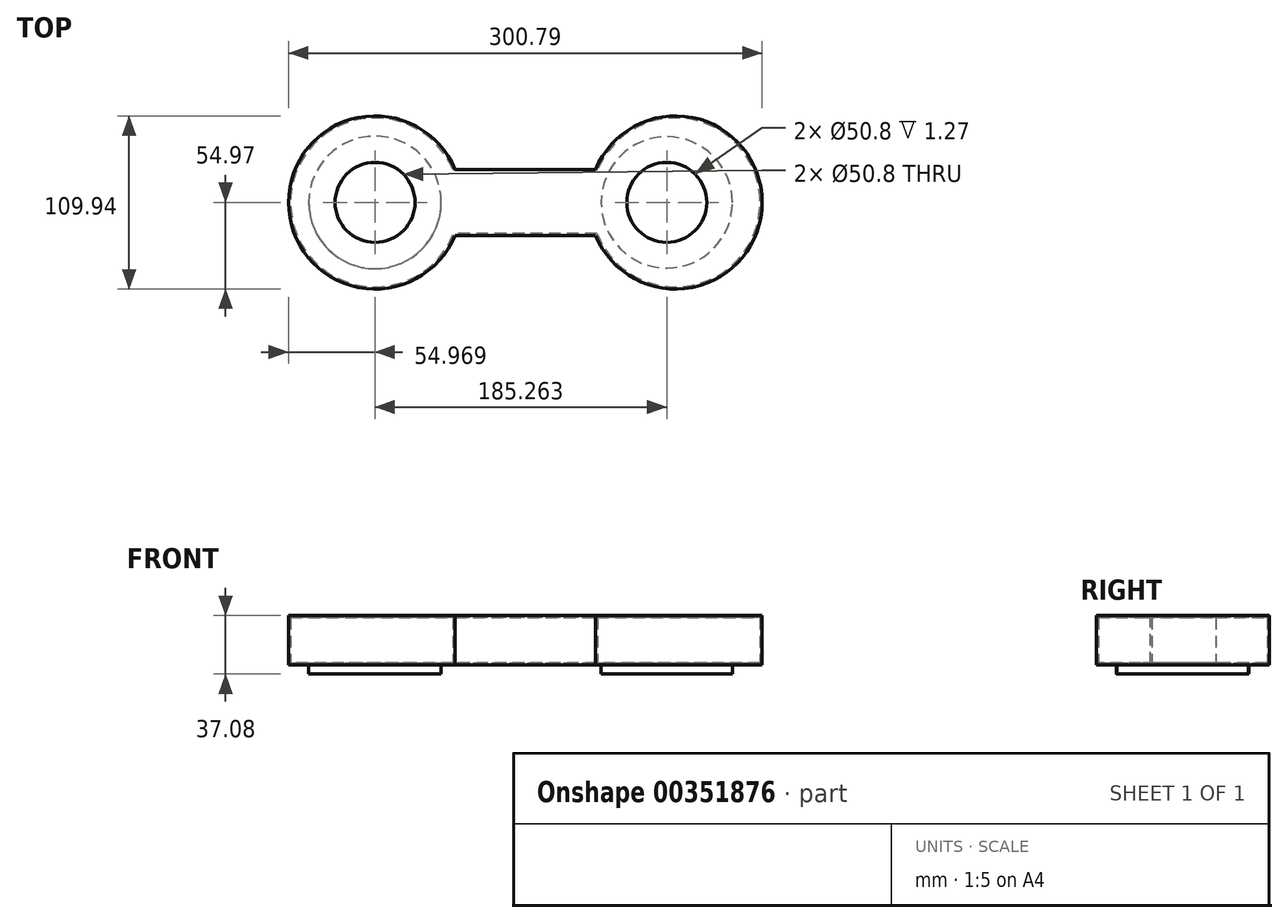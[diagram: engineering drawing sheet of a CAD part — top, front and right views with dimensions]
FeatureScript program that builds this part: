
annotation { "Feature Type Name" : "Feature", "Feature Type Description" : "" }
export const myFeature = defineFeature(function(context is Context, id is Id, definition is map)
    precondition{}
    {
        {
            var Q0;
            Q0=qCreatedBy(makeId("Top.planeOp"),FACE);
            var sketch = newSketch(context, id + "F0", { "sketchPlane" : qUnion([Q0])});
            skCircle(sketch, "E0", {"center": v(-92.63, 0) * mm, "radius": 54.97 * mm});
            skCircle(sketch, "E1.MirrorC", {"center": v(98.22, 0) * mm, "radius": 54.97 * mm});
            skLineSegment(sketch, "E2", {"start": v(-61.85, 20.9) * mm, "end": v(61.85, 20.9) * mm});
            skLineSegment(sketch, "E3", {"start": v(59.82, 20.9) * mm, "end": v(59.82, -20.9) * mm});
            skLineSegment(sketch, "E4", {"start": v(61.85, -20.9) * mm, "end": v(-61.85, -20.9) * mm});
            skLineSegment(sketch, "E5", {"start": v(-51.43, -20.9) * mm, "end": v(-51.43, 20.9) * mm});
            skSolve(sketch);
        }
        {
            var Q0;
            {var subQ0=sQuery(id+"F0.wireOp",EDGE,"E5");Q0=makeQuery(id+"F0.imprint","IMPRINT",FACE,{"disambiguationData":[TD([[makeQuery(id+"F0.imprint","IMPRINT",EDGE,{"derivedFrom":subQ0}),1.0]])]});}
            var Q1;
            {var subQ1=sQuery(id+"F0.wireOp",EDGE,"E2");Q1=makeQuery(id+"F0.imprint","IMPRINT",FACE,{"disambiguationData":[TD([[makeQuery(id+"F0.imprint","IMPRINT",EDGE,{"derivedFrom":subQ1}),-1.0]])]});}
            var Q2;
            {var subQ0=sQuery(id+"F0.wireOp",EDGE,"E3");Q2=makeQuery(id+"F0.imprint","IMPRINT",FACE,{"disambiguationData":[TD([[makeQuery(id+"F0.imprint","IMPRINT",EDGE,{"derivedFrom":subQ0}),1.0]])]});}
            var Q3;
            {var subQ0=sQuery(id+"F0.wireOp",EDGE,"E3");Q3=makeQuery(id+"F0.imprint","IMPRINT",FACE,{"disambiguationData":[TD([[makeQuery(id+"F0.imprint","IMPRINT",EDGE,{"derivedFrom":subQ0}),-1.0]])]});}
            var Q4;
            {var subQ0=sQuery(id+"F0.wireOp",EDGE,"E5");Q4=makeQuery(id+"F0.imprint","IMPRINT",FACE,{"disambiguationData":[TD([[makeQuery(id+"F0.imprint","IMPRINT",EDGE,{"derivedFrom":subQ0}),-1.0]])]});}
            extrude(context, id + "F1", {"entities" : qUnion([Q0, Q1, Q2, Q3, Q4]), "depth" : 31.24 * mm});
        }
        {
            var Q0;
            Q0=makeQuery(id+"F1.opExtrude","SWEPT_FACE",FACE,{"disambiguationData":[OSD([sQuery(id+"F0.wireOp",EDGE,"E2")])]});
            shell(context, id + "F2", {"entities" : qUnion([Q0]), "thickness" : 1.27 * mm});
        }
        {
            var Q0;
            Q0=makeQuery(id+"F1.opExtrude","CAP_FACE",FACE,{"disambiguationData":[OSD([sQuery(id+"F0.wireOp",EDGE,"E0"),sQuery(id+"F0.wireOp",EDGE,"E1.MirrorC"),sQuery(id+"F0.wireOp",EDGE,"E2"),sQuery(id+"F0.wireOp",EDGE,"E4")])],"isStart":false});
            var sketch = newSketch(context, id + "F3", { "sketchPlane" : qUnion([Q0])});
            skPoint(sketch, "E6", {"position": v(-92.63, 0) * mm});
            skPoint(sketch, "E7.MirrorP", {"position": v(92.63, 0) * mm});
            skSolve(sketch);
        }
        {
            var Q0;
            Q0=sQuery(id+"F3.wireOp",VERTEX,"E6");
            var Q1;
            Q1=sQuery(id+"F3.wireOp",VERTEX,"E7.MirrorP");
            var Q2;
            Q2=makeQuery(id+"F1.opExtrude","SWEPT_BODY",BODY,{"disambiguationData":[OSD([sQuery(id+"F0.wireOp",EDGE,"E0"),sQuery(id+"F0.wireOp",EDGE,"E1.MirrorC"),sQuery(id+"F0.wireOp",EDGE,"E2"),sQuery(id+"F0.wireOp",EDGE,"E4")])]});
            hole(context, id + "F4", {"style" : HoleStyle.SIMPLE, "endStyle" : HoleEndStyle.THROUGH, "holeDiameter" : 50.8 * mm, "isTappedThrough" : true, "tappedDepth" : 12.7 * mm, "tapClearance" : 3, "locations" : qUnion([Q0, Q1]), "scope" : qUnion([Q2])});
        }
        {
            var Q0;
            Q0=makeQuery(id+"F1.opExtrude","CAP_FACE",FACE,{"disambiguationData":[OSD([sQuery(id+"F0.wireOp",EDGE,"E0"),sQuery(id+"F0.wireOp",EDGE,"E1.MirrorC"),sQuery(id+"F0.wireOp",EDGE,"E2"),sQuery(id+"F0.wireOp",EDGE,"E4")])],"isStart":true});
            var sketch = newSketch(context, id + "F5", { "sketchPlane" : qUnion([Q0])});
            skCircle(sketch, "E8", {"center": v(92.63, 0) * mm, "radius": 41.7 * mm});
            skCircle(sketch, "E9", {"center": v(-92.63, 0) * mm, "radius": 42.07 * mm});
            skSolve(sketch);
        }
        {
            var Q0;
            Q0 = qSketchRegion(id + "F5", true);
            extrude(context, id + "F6", {"entities" : qUnion([Q0]), "operationType" : NewBodyOperationType.ADD, "depth" : 5.84 * mm});
        }
    });
